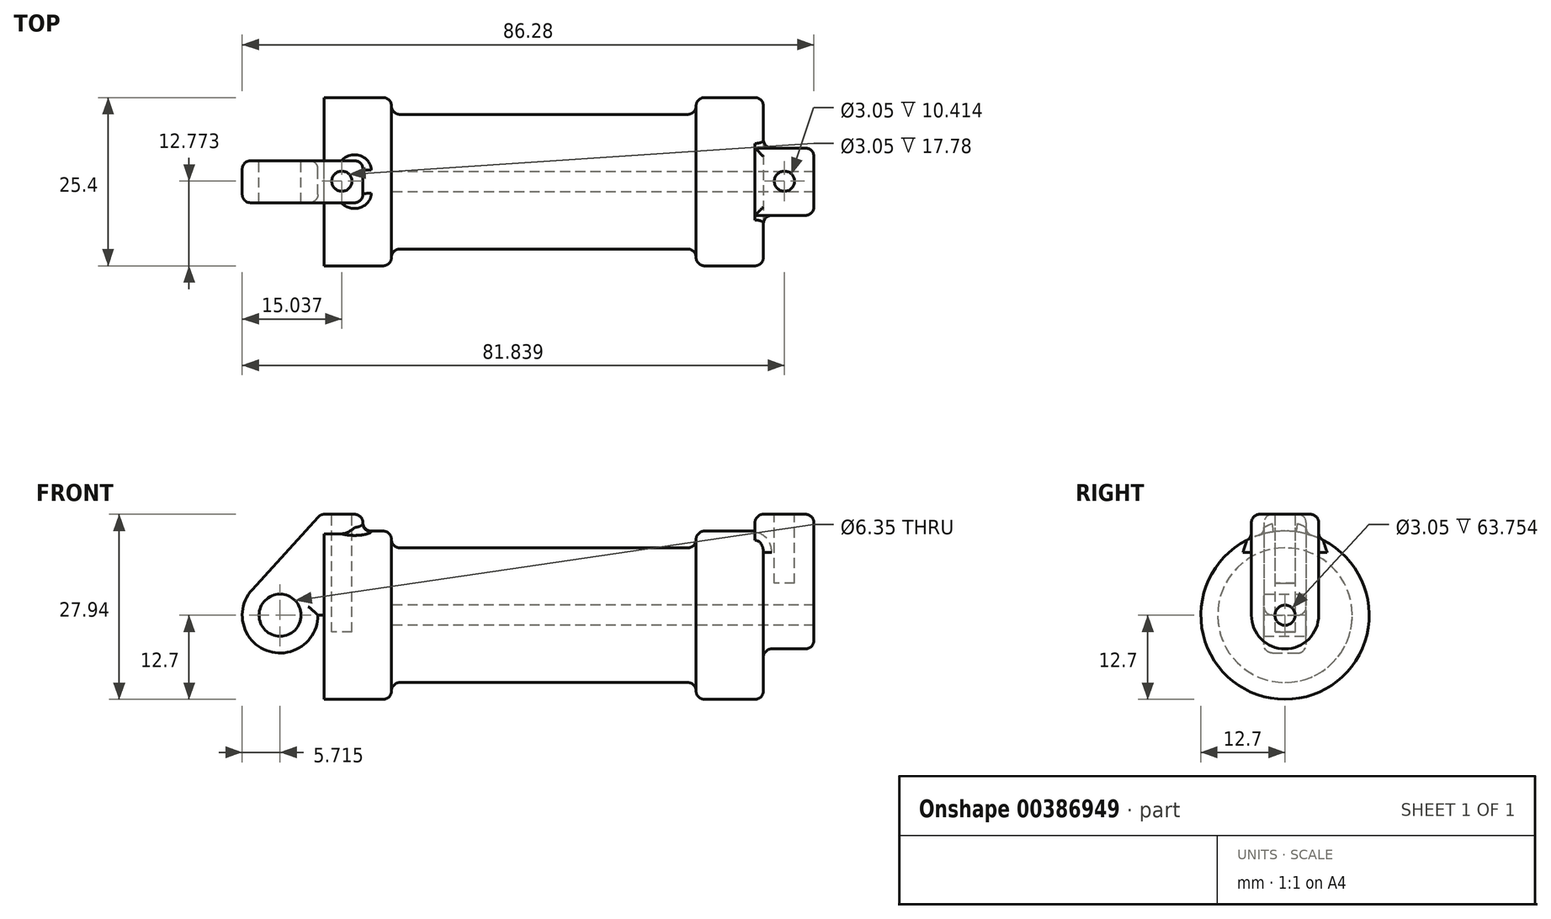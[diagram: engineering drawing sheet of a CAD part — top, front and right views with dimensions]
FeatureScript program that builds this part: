
annotation { "Feature Type Name" : "Feature", "Feature Type Description" : "" }
export const myFeature = defineFeature(function(context is Context, id is Id, definition is map)
    precondition{}
    {
        {
            var Q0;
            Q0=qCreatedBy(makeId("Front.planeOp"),FACE);
            var sketch = newSketch(context, id + "F0", { "sketchPlane" : qUnion([Q0])});
            skLineSegment(sketch, "E0", {"start": v(0, 0) * mm, "end": v(0, 12.7) * mm});
            skLineSegment(sketch, "E1", {"start": v(0, 12.7) * mm, "end": v(10.16, 12.7) * mm});
            skLineSegment(sketch, "E2", {"start": v(10.16, 12.7) * mm, "end": v(10.16, 10.16) * mm});
            skLineSegment(sketch, "E3", {"start": v(10.16, 10.16) * mm, "end": v(56.13, 10.16) * mm});
            skLineSegment(sketch, "E4", {"start": v(56.13, 10.16) * mm, "end": v(56.13, 12.7) * mm});
            skLineSegment(sketch, "E5", {"start": v(56.13, 12.7) * mm, "end": v(66.3, 12.7) * mm});
            skLineSegment(sketch, "E6", {"start": v(66.3, 12.7) * mm, "end": v(66.3, 0) * mm});
            skLineSegment(sketch, "E7", {"start": v(66.3, 0) * mm, "end": v(0, 0) * mm});
            skLineSegment(sketch, "E8", {"start": v(5.84, 15.24) * mm, "end": v(-0.5, 15.24) * mm});
            skLineSegment(sketch, "E9", {"start": v(-0.5, 15.24) * mm, "end": v(-10.88, 3.85) * mm});
            skLineSegment(sketch, "E10", {"start": v(0, 0) * mm, "end": v(-6.65, 0) * mm});
            skCircle(sketch, "E11", {"center": v(-6.65, 0) * mm, "radius": 5.72 * mm});
            skCircle(sketch, "E12", {"center": v(-6.65, 0) * mm, "radius": 3.18 * mm});
            skLineSegment(sketch, "E13", {"start": v(5.84, 15.24) * mm, "end": v(5.84, -9.4) * mm});
            skLineSegment(sketch, "E14", {"start": v(5.84, -9.4) * mm, "end": v(-8.18, -5.5) * mm});
            skSolve(sketch);
        }
        {
            var Q0;
            {var subQ0=sQuery(id+"F0.wireOp",EDGE,"E2");Q0=makeQuery(id+"F0.imprint","IMPRINT",FACE,{"disambiguationData":[TD([[makeQuery(id+"F0.imprint","IMPRINT",EDGE,{"derivedFrom":subQ0}),-1.0]])]});}
            var Q1;
            {var subQ0=sQuery(id+"F0.wireOp",EDGE,"E0");Q1=makeQuery(id+"F0.imprint","IMPRINT",FACE,{"disambiguationData":[TD([[makeQuery(id+"F0.imprint","IMPRINT",EDGE,{"derivedFrom":subQ0}),-1.0]])]});}
            var Q2;
            Q2=sQuery(id+"F0.wireOp",EDGE,"E7");
            revolve(context, id + "F1", {"entities" : qUnion([Q0, Q1]), "axis" : qUnion([Q2]), "revolveType" : RevolveType.FULL});
        }
        {
            var Q0;
            {var subQ0=sQuery(id+"F0.wireOp",EDGE,"E0");Q0=makeQuery(id+"F0.imprint","IMPRINT",FACE,{"disambiguationData":[TD([[makeQuery(id+"F0.imprint","IMPRINT",EDGE,{"derivedFrom":subQ0}),-1.0]])]});}
            var Q1;
            {var subQ1=sQuery(id+"F0.wireOp",EDGE,"E0");Q1=makeQuery(id+"F0.imprint","IMPRINT",FACE,{"disambiguationData":[TD([[makeQuery(id+"F0.imprint","IMPRINT",EDGE,{"derivedFrom":subQ1}),1.0]])]});}
            var Q2;
            {var subQ5=sQuery(id+"F0.wireOp",EDGE,"E12");Q2=makeQuery(id+"F0.imprint","IMPRINT",FACE,{"disambiguationData":[TD([[makeQuery(id+"F0.imprint","IMPRINT",EDGE,{"derivedFrom":subQ5}),-1.0]])]});}
            extrude(context, id + "F2", {"entities" : qUnion([Q0, Q1, Q2]), "operationType" : NewBodyOperationType.ADD, "depth" : 3.17 * mm, "hasSecondDirection" : true, "secondDirectionOppositeDirection" : true, "secondDirectionDepth" : 3.17 * mm});
        }
        {
            var Q0;
            Q0=makeQuery(id+"F1.opRevolve","SWEPT_FACE",FACE,{"disambiguationData":[OSD([sQuery(id+"F0.wireOp",EDGE,"E6")])]});
            var sketch = newSketch(context, id + "F3", { "sketchPlane" : qUnion([Q0])});
            skCircle(sketch, "E15", {"center": v(0, 0) * mm, "radius": 5.08 * mm});
            skCircle(sketch, "E16", {"center": v(0, 0) * mm, "radius": 1.52 * mm});
            skLineSegment(sketch, "E17", {"start": v(0, 0) * mm, "end": v(-5.08, 0) * mm, "construction": true});
            skLineSegment(sketch, "E18", {"start": v(0, 0) * mm, "end": v(5.08, 0) * mm, "construction": true});
            skLineSegment(sketch, "E19", {"start": v(5.08, 0) * mm, "end": v(5.08, 15.24) * mm});
            skLineSegment(sketch, "E20", {"start": v(-5.08, 15.24) * mm, "end": v(-5.08, 0) * mm});
            skLineSegment(sketch, "E21", {"start": v(-5.08, 15.24) * mm, "end": v(5.08, 15.24) * mm});
            skSolve(sketch);
        }
        {
            var Q0;
            Q0=qSketchRegion(id+"F3",true);
            extrude(context, id + "F4", {"entities" : qUnion([Q0]), "operationType" : NewBodyOperationType.ADD, "depth" : 7.62 * mm, "hasSecondDirection" : true, "secondDirectionOppositeDirection" : true, "secondDirectionDepth" : 1.27 * mm});
        }
        {
            var Q0;
            Q0=makeQuery(id+"F4.boolean.opBoolean","SPLIT",FACE,{"disambiguationData":[TD([makeQuery(id+"F4.opExtrude","SWEPT_FACE",FACE,{"disambiguationData":[OSD([sQuery(id+"F3.wireOp",EDGE,"E16")])]})])],"derivedFrom":makeQuery(id+"F1.opRevolve","SWEPT_FACE",FACE,{"disambiguationData":[OSD([sQuery(id+"F0.wireOp",EDGE,"E6")])]})});
            var Q1;
            Q1=makeQuery(id+"F1.opRevolve","SWEPT_FACE",FACE,{"disambiguationData":[OSD([sQuery(id+"F0.wireOp",EDGE,"E2")])]});
            extrude(context, id + "F5", {"entities" : qUnion([Q0]), "operationType" : NewBodyOperationType.REMOVE, "endBound" : BoundingType.UP_TO_SURFACE, "oppositeDirection" : true, "endBoundEntityFace" : qUnion([Q1]), "depth" : 25.4 * mm});
        }
        {
            var Q0;
            Q0=makeQuery(id+"F2.opExtrude","SWEPT_FACE",FACE,{"disambiguationData":[OSD([sQuery(id+"F0.wireOp",EDGE,"E8")])]});
            var sketch = newSketch(context, id + "F6", { "sketchPlane" : qUnion([Q0])});
            skCircle(sketch, "E22", {"center": v(2.67, 0.07) * mm, "radius": 1.52 * mm});
            skPoint(sketch, "E22.centerSnap0", {"position": v(2.67, 3.18) * mm});
            skSolve(sketch);
        }
        {
            var Q0;
            Q0=makeQuery(id+"F4.opExtrude","SWEPT_FACE",FACE,{"disambiguationData":[OSD([sQuery(id+"F3.wireOp",EDGE,"E21")])]});
            var sketch = newSketch(context, id + "F7", { "sketchPlane" : qUnion([Q0])});
            skCircle(sketch, "E23", {"center": v(69.47, 0.07) * mm, "radius": 1.52 * mm});
            skPoint(sketch, "E23.centerSnap0", {"position": v(69.47, 5.08) * mm});
            skSolve(sketch);
        }
        {
            var Q0;
            Q0 = qSketchRegion(id + "F7", true);
            extrude(context, id + "F8", {"entities" : qUnion([Q0]), "operationType" : NewBodyOperationType.REMOVE, "oppositeDirection" : true, "depth" : 10.4 * mm});
        }
        {
            var Q0;
            Q0 = qSketchRegion(id + "F6", true);
            extrude(context, id + "F9", {"entities" : qUnion([Q0]), "operationType" : NewBodyOperationType.REMOVE, "oppositeDirection" : true, "depth" : 17.78 * mm});
        }
        {
            var Q0;
            Q0=makeQuery(id+"F1.opRevolve","SWEPT_EDGE",EDGE,{"disambiguationData":[OSD([sQuery(id+"F0.wireOp",EDGE,"E2"),sQuery(id+"F0.wireOp",EDGE,"E3")])]});
            var Q1;
            Q1=makeQuery(id+"F1.opRevolve","SWEPT_EDGE",EDGE,{"disambiguationData":[OSD([sQuery(id+"F0.wireOp",EDGE,"E1"),sQuery(id+"F0.wireOp",EDGE,"E2")])]});
            var Q2;
            Q2=makeQuery(id+"F1.opRevolve","SWEPT_EDGE",EDGE,{"disambiguationData":[OSD([sQuery(id+"F0.wireOp",EDGE,"E3"),sQuery(id+"F0.wireOp",EDGE,"E4")])]});
            var Q3;
            Q3=makeQuery(id+"F1.opRevolve","SWEPT_EDGE",EDGE,{"disambiguationData":[OSD([sQuery(id+"F0.wireOp",EDGE,"E5"),sQuery(id+"F0.wireOp",EDGE,"E6")])]});
            var Q4;
            Q4=makeQuery(id+"F4.boolean.opBoolean","INTERSECT",EDGE,{"derivedFrom":[makeQuery(id+"F1.opRevolve","SWEPT_FACE",FACE,{"disambiguationData":[OSD([sQuery(id+"F0.wireOp",EDGE,"E6")])]}),makeQuery(id+"F4.opExtrude","SWEPT_FACE",FACE,{"disambiguationData":[OSD([sQuery(id+"F3.wireOp",EDGE,"E20")])]})]});
            var Q5;
            Q5=makeQuery(id+"F4.opExtrude","CAP_EDGE",EDGE,{"disambiguationData":[OSD([sQuery(id+"F3.wireOp",EDGE,"E20")])],"isStart":false});
            var Q6;
            Q6=makeQuery(id+"F4.opExtrude","CAP_EDGE",EDGE,{"disambiguationData":[OSD([sQuery(id+"F3.wireOp",EDGE,"E21")])],"isStart":false});
            var Q7;
            Q7=makeQuery(id+"F4.opExtrude","CAP_EDGE",EDGE,{"disambiguationData":[OSD([sQuery(id+"F3.wireOp",EDGE,"E21")])],"isStart":true});
            var Q8;
            Q8=makeQuery(id+"F4.opExtrude","SWEPT_EDGE",EDGE,{"disambiguationData":[OSD([sQuery(id+"F3.wireOp",EDGE,"E19"),sQuery(id+"F3.wireOp",EDGE,"E21")])]});
            var Q9;
            Q9=makeQuery(id+"F4.opExtrude","SWEPT_EDGE",EDGE,{"disambiguationData":[OSD([sQuery(id+"F3.wireOp",EDGE,"E20"),sQuery(id+"F3.wireOp",EDGE,"E21")])]});
            var Q10;
            Q10=makeQuery(id+"F1.opRevolve","SWEPT_EDGE",EDGE,{"disambiguationData":[OSD([sQuery(id+"F0.wireOp",EDGE,"E4"),sQuery(id+"F0.wireOp",EDGE,"E5")])]});
            var Q11;
            Q11=makeQuery(id+"F2.boolean.opBoolean","INTERSECT",EDGE,{"derivedFrom":[makeQuery(id+"F1.opRevolve","SWEPT_FACE",FACE,{"disambiguationData":[OSD([sQuery(id+"F0.wireOp",EDGE,"E1")])]}),makeQuery(id+"F2.opExtrude","SWEPT_FACE",FACE,{"disambiguationData":[OSD([sQuery(id+"F0.wireOp",EDGE,"E13")])]})]});
            var Q12;
            Q12=makeQuery(id+"F2.opExtrude","SWEPT_FACE",FACE,{"disambiguationData":[OSD([sQuery(id+"F0.wireOp",EDGE,"E13")])]});
            var Q13;
            Q13=makeQuery(id+"F2.opExtrude","CAP_EDGE",EDGE,{"disambiguationData":[OSD([sQuery(id+"F0.wireOp",EDGE,"E8")])],"isStart":true});
            var Q14;
            Q14=makeQuery(id+"F2.opExtrude","SWEPT_EDGE",EDGE,{"disambiguationData":[OSD([sQuery(id+"F0.wireOp",EDGE,"E8"),sQuery(id+"F0.wireOp",EDGE,"E9")])]});
            var Q15;
            Q15=makeQuery(id+"F2.opExtrude","CAP_EDGE",EDGE,{"disambiguationData":[OSD([sQuery(id+"F0.wireOp",EDGE,"E8")])],"isStart":false});
            var Q16;
            Q16=makeQuery(id+"F2.opExtrude","CAP_EDGE",EDGE,{"disambiguationData":[OSD([sQuery(id+"F0.wireOp",EDGE,"E9")])],"isStart":true});
            var Q17;
            Q17=makeQuery(id+"F2.opExtrude","CAP_EDGE",EDGE,{"disambiguationData":[OSD([sQuery(id+"F0.wireOp",EDGE,"E9")])],"isStart":false});
            var Q18;
            Q18=makeQuery(id+"F2.opExtrude","CAP_EDGE",EDGE,{"disambiguationData":[OSD([sQuery(id+"F0.wireOp",EDGE,"E7"),sQuery(id+"F0.wireOp",EDGE,"E10")])],"isStart":true});
            var Q19;
            Q19=makeQuery(id+"F2.opExtrude","CAP_EDGE",EDGE,{"disambiguationData":[OSD([sQuery(id+"F0.wireOp",EDGE,"E7"),sQuery(id+"F0.wireOp",EDGE,"E10")])],"isStart":false});
            fillet(context, id + "F10", {"entities" : qUnion([Q0, Q1, Q2, Q3, Q4, Q5, Q6, Q7, Q8, Q9, Q10, Q11, Q12, Q13, Q14, Q15, Q16, Q17, Q18, Q19]), "radius" : 1.27 * mm, "tangentPropagation" : true, "allowEdgeOverflow" : false});
        }
    });
